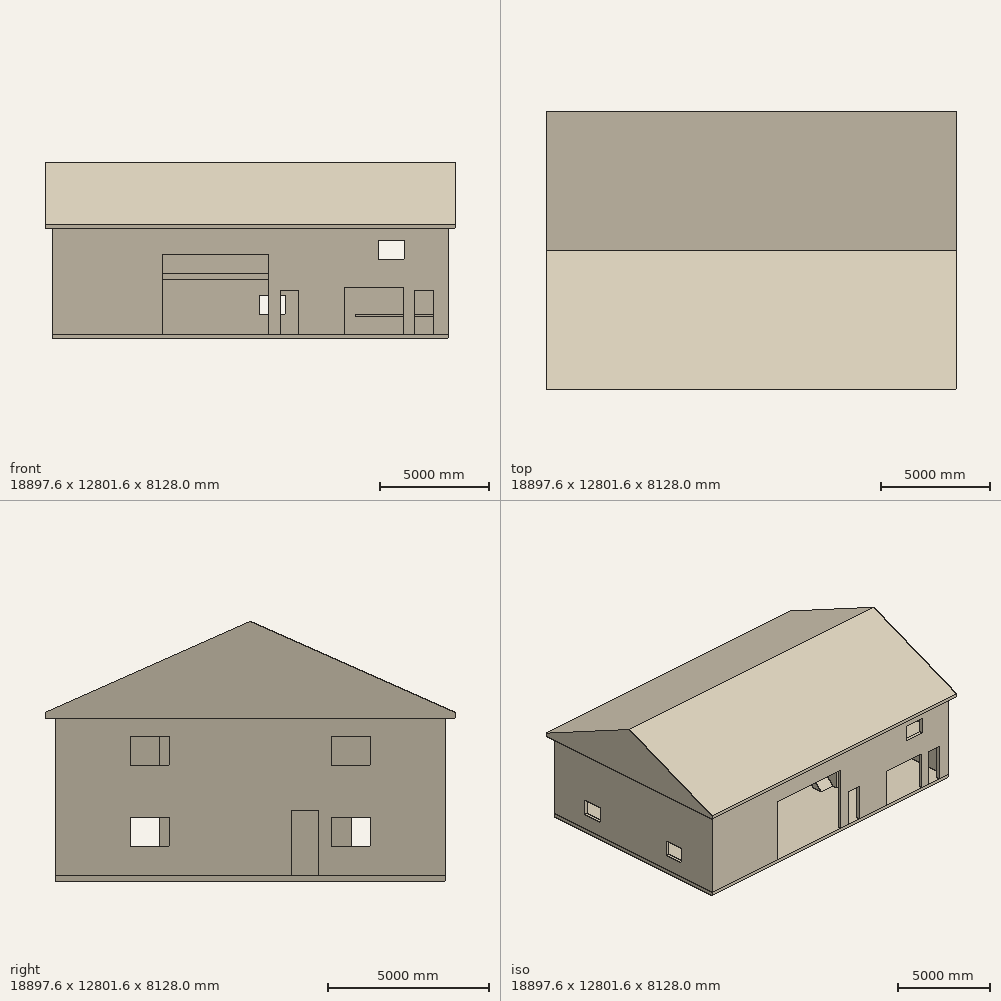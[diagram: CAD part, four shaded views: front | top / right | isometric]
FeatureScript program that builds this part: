
annotation { "Feature Type Name" : "Feature", "Feature Type Description" : "" }
export const myFeature = defineFeature(function(context is Context, id is Id, definition is map)
    precondition{}
    {
        {
            var Q0;
            Q0=qCreatedBy(makeId("Top.planeOp"),FACE);
            var sketch = newSketch(context, id + "F0", { "sketchPlane" : qUnion([Q0])});
            skLineSegment(sketch, "E0.bottom", {"start": v(-9144, 6096) * mm, "end": v(9144, 6096) * mm});
            skLineSegment(sketch, "E0.top", {"start": v(-9144, -6096) * mm, "end": v(9144, -6096) * mm});
            skLineSegment(sketch, "E0.left", {"start": v(-9144, 6096) * mm, "end": v(-9144, -6096) * mm});
            skLineSegment(sketch, "E0.right", {"start": v(9144, 6096) * mm, "end": v(9144, -6096) * mm});
            skLineSegment(sketch, "E1", {"start": v(-9144, 6096) * mm, "end": v(9144, -6096) * mm, "construction": true});
            skSolve(sketch);
        }
        {
            var Q0;
            Q0=makeQuery(id+"F0.imprint","IMPRINT",FACE,{"disambiguationData":[TD([[makeQuery(id+"F0.imprint","IMPRINT",EDGE,{"derivedFrom":sQuery(id+"F0.wireOp",EDGE,"E0.bottom")}),-1.0]])]});
            extrude(context, id + "F1", {"entities" : qUnion([Q0]), "depth" : 203.2 * mm, "offsetDistance" : 25.4 * mm});
        }
        {
            var Q0;
            Q0=makeQuery(id+"F1.opExtrude","CAP_FACE",FACE,{"disambiguationData":[OSD([sQuery(id+"F0.wireOp",EDGE,"E0.bottom"),sQuery(id+"F0.wireOp",EDGE,"E0.top"),sQuery(id+"F0.wireOp",EDGE,"E0.left"),sQuery(id+"F0.wireOp",EDGE,"E0.right")])],"isStart":false});
            var sketch = newSketch(context, id + "F2", { "sketchPlane" : qUnion([Q0])});
            skLineSegment(sketch, "E2.0", {"start": v(-9144, 6096) * mm, "end": v(9144, 6096) * mm});
            skLineSegment(sketch, "E2.1", {"start": v(-9144, 6096) * mm, "end": v(-9144, -6096) * mm});
            skLineSegment(sketch, "E2.2", {"start": v(-9144, -6096) * mm, "end": v(9144, -6096) * mm});
            skLineSegment(sketch, "E2.3", {"start": v(9144, 6096) * mm, "end": v(9144, -6096) * mm});
            skLineSegment(sketch, "E3.0", {"start": v(-8940.8, 5892.8) * mm, "end": v(8940.8, 5892.8) * mm});
            skLineSegment(sketch, "E3.1", {"start": v(-8940.8, 5892.8) * mm, "end": v(-8940.8, -5892.8) * mm});
            skLineSegment(sketch, "E3.2", {"start": v(-8940.8, -5892.8) * mm, "end": v(8940.8, -5892.8) * mm});
            skLineSegment(sketch, "E3.3", {"start": v(8940.8, 5892.8) * mm, "end": v(8940.8, -5892.8) * mm});
            skSolve(sketch);
        }
        {
            var Q0;
            Q0=qSketchRegion(id+"F2",true);
            extrude(context, id + "F3", {"entities" : qUnion([Q0]), "depth" : 4876.8 * mm, "offsetDistance" : 25.4 * mm});
        }
        {
            var Q0;
            Q0=qCreatedBy(makeId("Right.planeOp"),FACE);
            var sketch = newSketch(context, id + "F4", { "sketchPlane" : qUnion([Q0])});
            skLineSegment(sketch, "E4.0", {"start": v(6400.8, 5080) * mm, "end": v(-6400.8, 5080) * mm});
            skLineSegment(sketch, "E5", {"start": v(-6400.8, 5080) * mm, "end": v(-6400.8, 5283.2) * mm});
            skLineSegment(sketch, "E6", {"start": v(-6400.8, 5283.2) * mm, "end": v(0, 8128) * mm});
            skLineSegment(sketch, "E7", {"start": v(0, 8128) * mm, "end": v(6400.8, 5283.2) * mm});
            skLineSegment(sketch, "E8", {"start": v(6400.8, 5283.2) * mm, "end": v(6400.8, 5080) * mm});
            skSolve(sketch);
        }
        {
            var Q0;
            Q0=qSketchRegion(id+"F4",true);
            var Q1;
            Q1=makeQuery(id+"F3.opExtrude","SWEPT_FACE",FACE,{"disambiguationData":[OSD([sQuery(id+"F2.wireOp",EDGE,"E2.3")])]});
            var Q2;
            Q2=makeQuery(id+"F3.opExtrude","SWEPT_FACE",FACE,{"disambiguationData":[OSD([sQuery(id+"F2.wireOp",EDGE,"E2.1")])]});
            extrude(context, id + "F5", {"entities" : qUnion([Q0]), "endBound" : BoundingType.UP_TO_SURFACE, "depth" : 25.4 * mm, "endBoundEntityFace" : qUnion([Q1]), "hasOffset" : true, "offsetDistance" : -304.8 * mm, "hasSecondDirection" : true, "secondDirectionBound" : SecondDirectionBoundingType.UP_TO_SURFACE, "secondDirectionOppositeDirection" : true, "secondDirectionDepth" : 25.4 * mm, "secondDirectionBoundEntityFace" : qUnion([Q2]), "hasSecondDirectionOffset" : true, "secondDirectionOffsetDistance" : -304.8 * mm});
        }
        {
            var Q0;
            Q0=makeQuery(id+"F1.opExtrude","CAP_FACE",FACE,{"disambiguationData":[OSD([sQuery(id+"F0.wireOp",EDGE,"E0.bottom"),sQuery(id+"F0.wireOp",EDGE,"E0.top"),sQuery(id+"F0.wireOp",EDGE,"E0.left"),sQuery(id+"F0.wireOp",EDGE,"E0.right")])],"isStart":false});
            var sketch = newSketch(context, id + "F6", { "sketchPlane" : qUnion([Q0])});
            skLineSegment(sketch, "E9", {"start": v(3759.2, -5892.8) * mm, "end": v(3759.2, 5892.8) * mm});
            skLineSegment(sketch, "E10.0", {"start": v(3911.6, -5892.8) * mm, "end": v(3911.6, 203.2) * mm});
            skLineSegment(sketch, "E11", {"start": v(3911.6, 355.6) * mm, "end": v(8940.8, 355.6) * mm});
            skLineSegment(sketch, "E12.0", {"start": v(3911.6, 203.2) * mm, "end": v(8940.8, 203.2) * mm});
            skLineSegment(sketch, "E13.trimOffspring", {"start": v(3911.6, 355.6) * mm, "end": v(3911.6, 5892.8) * mm});
            skLineSegment(sketch, "E14", {"start": v(3759.2, -5892.8) * mm, "end": v(3911.6, -5892.8) * mm});
            skLineSegment(sketch, "E15", {"start": v(3759.2, 5892.8) * mm, "end": v(3911.6, 5892.8) * mm});
            skLineSegment(sketch, "E16", {"start": v(8940.8, 355.6) * mm, "end": v(8940.8, 203.2) * mm});
            skSolve(sketch);
        }
        {
            var Q0;
            Q0=qSketchRegion(id+"F6",true);
            extrude(context, id + "F7", {"entities" : qUnion([Q0]), "depth" : 2336.8 * mm, "offsetDistance" : 25.4 * mm});
        }
        {
            var Q0;
            Q0=makeQuery(id+"F7.opExtrude","CAP_FACE",FACE,{"disambiguationData":[OSD([sQuery(id+"F6.wireOp",EDGE,"E9"),sQuery(id+"F6.wireOp",EDGE,"E10.0"),sQuery(id+"F6.wireOp",EDGE,"E11"),sQuery(id+"F6.wireOp",EDGE,"E12.0"),sQuery(id+"F6.wireOp",EDGE,"E13.trimOffspring"),sQuery(id+"F6.wireOp",EDGE,"E14"),sQuery(id+"F6.wireOp",EDGE,"E15"),sQuery(id+"F6.wireOp",EDGE,"E16")])],"isStart":false});
            var sketch = newSketch(context, id + "F8", { "sketchPlane" : qUnion([Q0])});
            skLineSegment(sketch, "E17.0", {"start": v(3759.2, -5892.8) * mm, "end": v(3759.2, 5892.8) * mm});
            skLineSegment(sketch, "E18.0", {"start": v(8940.8, 5892.8) * mm, "end": v(8940.8, -5892.8) * mm});
            skLineSegment(sketch, "E19.0", {"start": v(3759.2, 5892.8) * mm, "end": v(8940.8, 5892.8) * mm});
            skLineSegment(sketch, "E20.0", {"start": v(3759.2, -5892.8) * mm, "end": v(8940.8, -5892.8) * mm});
            skPoint(sketch, "E21.orphan", {"position": v(-8940.8, -5892.8) * mm});
            skPoint(sketch, "E22.orphan", {"position": v(-8940.8, 5892.8) * mm});
            skSolve(sketch);
        }
        {
            var Q0;
            Q0=qSketchRegion(id+"F8",true);
            extrude(context, id + "F9", {"entities" : qUnion([Q0]), "depth" : 203.2 * mm, "offsetDistance" : 25.4 * mm});
        }
        {
            var Q0;
            Q0=makeQuery(id+"F3.opExtrude","SWEPT_FACE",FACE,{"disambiguationData":[OSD([sQuery(id+"F2.wireOp",EDGE,"E2.2")])]});
            var sketch = newSketch(context, id + "F10", { "sketchPlane" : qUnion([Q0])});
            skLineSegment(sketch, "E23.bottom", {"start": v(-4064, 203.2) * mm, "end": v(812.8, 203.2) * mm});
            skLineSegment(sketch, "E23.top", {"start": v(-4064, 3860.8) * mm, "end": v(812.8, 3860.8) * mm});
            skLineSegment(sketch, "E23.left", {"start": v(-4064, 203.2) * mm, "end": v(-4064, 3860.8) * mm});
            skLineSegment(sketch, "E23.right", {"start": v(812.8, 203.2) * mm, "end": v(812.8, 3860.8) * mm});
            skLineSegment(sketch, "E24.bottom", {"start": v(1371.6, 203.2) * mm, "end": v(2235.2, 203.2) * mm});
            skLineSegment(sketch, "E24.top", {"start": v(1371.6, 2235.2) * mm, "end": v(2235.2, 2235.2) * mm});
            skLineSegment(sketch, "E24.left", {"start": v(1371.6, 203.2) * mm, "end": v(1371.6, 2235.2) * mm});
            skLineSegment(sketch, "E24.right", {"start": v(2235.2, 203.2) * mm, "end": v(2235.2, 2235.2) * mm});
            skLineSegment(sketch, "E25.bottom", {"start": v(4318, 203.2) * mm, "end": v(7061.2, 203.2) * mm});
            skLineSegment(sketch, "E25.top", {"start": v(4318, 2336.8) * mm, "end": v(7061.2, 2336.8) * mm});
            skLineSegment(sketch, "E25.left", {"start": v(4318, 203.2) * mm, "end": v(4318, 2336.8) * mm});
            skLineSegment(sketch, "E25.right", {"start": v(7061.2, 203.2) * mm, "end": v(7061.2, 2336.8) * mm});
            skLineSegment(sketch, "E26.bottom", {"start": v(7569.2, 203.2) * mm, "end": v(8432.8, 203.2) * mm});
            skLineSegment(sketch, "E26.top", {"start": v(7569.2, 2235.2) * mm, "end": v(8432.8, 2235.2) * mm});
            skLineSegment(sketch, "E26.left", {"start": v(7569.2, 203.2) * mm, "end": v(7569.2, 2235.2) * mm});
            skLineSegment(sketch, "E26.right", {"start": v(8432.8, 203.2) * mm, "end": v(8432.8, 2235.2) * mm});
            skLineSegment(sketch, "E27.bottom", {"start": v(5892.8, 4546.6) * mm, "end": v(7112, 4546.6) * mm});
            skLineSegment(sketch, "E27.top", {"start": v(5892.8, 3632.2) * mm, "end": v(7112, 3632.2) * mm});
            skLineSegment(sketch, "E27.left", {"start": v(5892.8, 4546.6) * mm, "end": v(5892.8, 3632.2) * mm});
            skLineSegment(sketch, "E27.right", {"start": v(7112, 4546.6) * mm, "end": v(7112, 3632.2) * mm});
            skSolve(sketch);
        }
        {
            var Q0;
            Q0=qSketchRegion(id+"F10",true);
            extrude(context, id + "F11", {"entities" : qUnion([Q0]), "operationType" : NewBodyOperationType.REMOVE, "endBound" : BoundingType.UP_TO_NEXT, "oppositeDirection" : true, "depth" : 25.4 * mm, "offsetDistance" : 25.4 * mm});
        }
        {
            var Q0;
            Q0=makeQuery(id+"F3.opExtrude","SWEPT_FACE",FACE,{"disambiguationData":[OSD([sQuery(id+"F2.wireOp",EDGE,"E2.3")])]});
            var sketch = newSketch(context, id + "F12", { "sketchPlane" : qUnion([Q0])});
            skLineSegment(sketch, "E28.bottom", {"start": v(-5588, 203.2) * mm, "end": v(-4724.4, 203.2) * mm, "construction": true});
            skLineSegment(sketch, "E28.top", {"start": v(-5588, 2235.2) * mm, "end": v(-4724.4, 2235.2) * mm, "construction": true});
            skLineSegment(sketch, "E28.left", {"start": v(-5588, 203.2) * mm, "end": v(-5588, 2235.2) * mm, "construction": true});
            skLineSegment(sketch, "E28.right", {"start": v(-4724.4, 203.2) * mm, "end": v(-4724.4, 2235.2) * mm, "construction": true});
            skLineSegment(sketch, "E29.bottom", {"start": v(1270, 203.2) * mm, "end": v(2133.6, 203.2) * mm});
            skLineSegment(sketch, "E29.top", {"start": v(1270, 2235.2) * mm, "end": v(2133.6, 2235.2) * mm});
            skLineSegment(sketch, "E29.left", {"start": v(1270, 203.2) * mm, "end": v(1270, 2235.2) * mm});
            skLineSegment(sketch, "E29.right", {"start": v(2133.6, 203.2) * mm, "end": v(2133.6, 2235.2) * mm});
            skSolve(sketch);
        }
        {
            var Q0;
            Q0=qSketchRegion(id+"F12",true);
            extrude(context, id + "F13", {"entities" : qUnion([Q0]), "operationType" : NewBodyOperationType.REMOVE, "endBound" : BoundingType.UP_TO_NEXT, "oppositeDirection" : true, "depth" : 25.4 * mm, "offsetDistance" : 25.4 * mm});
        }
        {
            var Q0;
            Q0=makeQuery(id+"F7.opExtrude","SWEPT_FACE",FACE,{"disambiguationData":[OSD([sQuery(id+"F6.wireOp",EDGE,"E9")])]});
            var sketch = newSketch(context, id + "F14", { "sketchPlane" : qUnion([Q0])});
            skLineSegment(sketch, "E30", {"start": v(1965.26, 203.2) * mm, "end": v(-371.54, 2540) * mm});
            skLineSegment(sketch, "E31", {"start": v(0, 2743.2) * mm, "end": v(2540, 203.2) * mm});
            skLineSegment(sketch, "E32", {"start": v(-574.74, 2743.2) * mm, "end": v(0, 2743.2) * mm});
            skLineSegment(sketch, "E33", {"start": v(2540, 203.2) * mm, "end": v(1965.26, 203.2) * mm});
            skLineSegment(sketch, "E34.bottom", {"start": v(2955.8, 203.2) * mm, "end": v(5394.2, 203.2) * mm, "construction": true});
            skLineSegment(sketch, "E34.top", {"start": v(2955.8, 2336.8) * mm, "end": v(5394.2, 2336.8) * mm, "construction": true});
            skLineSegment(sketch, "E34.left", {"start": v(2955.8, 203.2) * mm, "end": v(2955.8, 2336.8) * mm, "construction": true});
            skLineSegment(sketch, "E34.right", {"start": v(5394.2, 203.2) * mm, "end": v(5394.2, 2336.8) * mm, "construction": true});
            skLineSegment(sketch, "E35.bottom", {"start": v(-4403.76, 203.2) * mm, "end": v(-1965.36, 203.2) * mm, "construction": true});
            skLineSegment(sketch, "E35.top", {"start": v(-4403.76, 2336.8) * mm, "end": v(-1965.36, 2336.8) * mm, "construction": true});
            skLineSegment(sketch, "E35.left", {"start": v(-4403.76, 203.2) * mm, "end": v(-4403.76, 2336.8) * mm, "construction": true});
            skLineSegment(sketch, "E35.right", {"start": v(-1965.36, 203.2) * mm, "end": v(-1965.36, 2336.8) * mm, "construction": true});
            skLineSegment(sketch, "E36", {"start": v(-1219.2, 2540) * mm, "end": v(-1219.2, 2743.2) * mm});
            skLineSegment(sketch, "E37", {"start": v(-1219.2, 2743.2) * mm, "end": v(-574.74, 2743.2) * mm});
            skLineSegment(sketch, "E38", {"start": v(-1219.2, 2540) * mm, "end": v(-371.54, 2540) * mm});
            skSolve(sketch);
        }
        {
            var Q0;
            Q0=qSketchRegion(id+"F14",true);
            extrude(context, id + "F15", {"entities" : qUnion([Q0]), "depth" : 914.4 * mm, "offsetDistance" : 25.4 * mm});
        }
        {
            var Q0;
            Q0=makeQuery(id+"F7.opExtrude","SWEPT_FACE",FACE,{"disambiguationData":[OSD([sQuery(id+"F6.wireOp",EDGE,"E9")])]});
            var sketch = newSketch(context, id + "F16", { "sketchPlane" : qUnion([Q0])});
            skLineSegment(sketch, "E39.bottom", {"start": v(-5588, 203.2) * mm, "end": v(-3149.6, 203.2) * mm});
            skLineSegment(sketch, "E39.top", {"start": v(-5588, 2336.8) * mm, "end": v(-3149.6, 2336.8) * mm});
            skLineSegment(sketch, "E39.left", {"start": v(-5588, 203.2) * mm, "end": v(-5588, 2336.8) * mm});
            skLineSegment(sketch, "E39.right", {"start": v(-3149.6, 203.2) * mm, "end": v(-3149.6, 2336.8) * mm});
            skLineSegment(sketch, "E40.bottom", {"start": v(2844.8, 203.2) * mm, "end": v(5283.2, 203.2) * mm});
            skLineSegment(sketch, "E40.top", {"start": v(2844.8, 2336.8) * mm, "end": v(5283.2, 2336.8) * mm});
            skLineSegment(sketch, "E40.left", {"start": v(2844.8, 203.2) * mm, "end": v(2844.8, 2336.8) * mm});
            skLineSegment(sketch, "E40.right", {"start": v(5283.2, 203.2) * mm, "end": v(5283.2, 2336.8) * mm});
            skSolve(sketch);
        }
        {
            var Q0;
            Q0=qSketchRegion(id+"F16",true);
            extrude(context, id + "F17", {"entities" : qUnion([Q0]), "operationType" : NewBodyOperationType.REMOVE, "endBound" : BoundingType.UP_TO_NEXT, "oppositeDirection" : true, "depth" : 25.4 * mm, "offsetDistance" : 25.4 * mm});
        }
        {
            var Q0;
            Q0=makeQuery(id+"F9.opExtrude","CAP_FACE",FACE,{"disambiguationData":[OSD([sQuery(id+"F8.wireOp",EDGE,"E17.0"),sQuery(id+"F8.wireOp",EDGE,"E18.0"),sQuery(id+"F8.wireOp",EDGE,"E19.0"),sQuery(id+"F8.wireOp",EDGE,"E20.0")])],"isStart":false});
            var sketch = newSketch(context, id + "F18", { "sketchPlane" : qUnion([Q0])});
            skLineSegment(sketch, "E41.0", {"start": v(3759.2, -5892.8) * mm, "end": v(3759.2, 5892.8) * mm});
            skLineSegment(sketch, "E42.0", {"start": v(3911.6, -5892.8) * mm, "end": v(3911.6, 5892.8) * mm});
            skLineSegment(sketch, "E43", {"start": v(3759.2, 5892.8) * mm, "end": v(3911.6, 5892.8) * mm});
            skLineSegment(sketch, "E44", {"start": v(3759.2, -5892.8) * mm, "end": v(3911.6, -5892.8) * mm});
            skSolve(sketch);
        }
        {
            var Q0;
            Q0=qSketchRegion(id+"F18",true);
            var Q1;
            Q1=makeQuery(id+"F3.opExtrude","CAP_FACE",FACE,{"disambiguationData":[OSD([sQuery(id+"F2.wireOp",EDGE,"E2.0"),sQuery(id+"F2.wireOp",EDGE,"E2.1"),sQuery(id+"F2.wireOp",EDGE,"E2.2"),sQuery(id+"F2.wireOp",EDGE,"E2.3"),sQuery(id+"F2.wireOp",EDGE,"E3.0"),sQuery(id+"F2.wireOp",EDGE,"E3.1"),sQuery(id+"F2.wireOp",EDGE,"E3.2"),sQuery(id+"F2.wireOp",EDGE,"E3.3")])],"isStart":false});
            extrude(context, id + "F19", {"entities" : qUnion([Q0]), "endBound" : BoundingType.UP_TO_SURFACE, "depth" : 25.4 * mm, "endBoundEntityFace" : qUnion([Q1]), "offsetDistance" : 25.4 * mm});
        }
        {
            var Q0;
            Q0=makeQuery(id+"F19.opExtrude","SWEPT_FACE",FACE,{"disambiguationData":[OSD([sQuery(id+"F18.wireOp",EDGE,"E41.0")])]});
            var sketch = newSketch(context, id + "F20", { "sketchPlane" : qUnion([Q0])});
            skLineSegment(sketch, "E45.bottom", {"start": v(-1219.2, 2743.2) * mm, "end": v(-355.6, 2743.2) * mm});
            skLineSegment(sketch, "E45.top", {"start": v(-1219.2, 4724.4) * mm, "end": v(-355.6, 4724.4) * mm});
            skLineSegment(sketch, "E45.left", {"start": v(-1219.2, 2743.2) * mm, "end": v(-1219.2, 4724.4) * mm});
            skLineSegment(sketch, "E45.right", {"start": v(-355.6, 2743.2) * mm, "end": v(-355.6, 4724.4) * mm});
            skLineSegment(sketch, "E46.bottom", {"start": v(2844.8, 2743.2) * mm, "end": v(5283.2, 2743.2) * mm});
            skLineSegment(sketch, "E46.top", {"start": v(2844.8, 4724.4) * mm, "end": v(5283.2, 4724.4) * mm});
            skLineSegment(sketch, "E46.left", {"start": v(2844.8, 2743.2) * mm, "end": v(2844.8, 4724.4) * mm});
            skLineSegment(sketch, "E46.right", {"start": v(5283.2, 2743.2) * mm, "end": v(5283.2, 4724.4) * mm});
            skSolve(sketch);
        }
        {
            var Q0;
            Q0=qSketchRegion(id+"F20",true);
            extrude(context, id + "F21", {"entities" : qUnion([Q0]), "operationType" : NewBodyOperationType.REMOVE, "endBound" : BoundingType.UP_TO_NEXT, "oppositeDirection" : true, "depth" : 25.4 * mm, "offsetDistance" : 25.4 * mm});
        }
        {
            var Q0;
            Q0=makeQuery(id+"F3.opExtrude","SWEPT_FACE",FACE,{"disambiguationData":[OSD([sQuery(id+"F2.wireOp",EDGE,"E3.0")])]});
            var sketch = newSketch(context, id + "F22", { "sketchPlane" : qUnion([Q0])});
            skLineSegment(sketch, "E47.bottom", {"start": v(-8940.8, 2997.2) * mm, "end": v(3759.2, 2997.2) * mm});
            skLineSegment(sketch, "E47.top", {"start": v(-8940.8, 2743.2) * mm, "end": v(3759.2, 2743.2) * mm});
            skLineSegment(sketch, "E47.left", {"start": v(-8940.8, 2997.2) * mm, "end": v(-8940.8, 2743.2) * mm});
            skLineSegment(sketch, "E47.right", {"start": v(3759.2, 2997.2) * mm, "end": v(3759.2, 2743.2) * mm});
            skSolve(sketch);
        }
        {
            var Q0;
            Q0=qSketchRegion(id+"F22",true);
            extrude(context, id + "F23", {"entities" : qUnion([Q0]), "depth" : 4572 * mm, "offsetDistance" : 25.4 * mm});
        }
        {
            var Q0;
            Q0=makeQuery(id+"F3.opExtrude","SWEPT_FACE",FACE,{"disambiguationData":[OSD([sQuery(id+"F2.wireOp",EDGE,"E3.1")])]});
            var sketch = newSketch(context, id + "F24", { "sketchPlane" : qUnion([Q0])});
            skLineSegment(sketch, "E48.bottom", {"start": v(5892.8, 3225.8) * mm, "end": v(-4064, 3225.8) * mm});
            skLineSegment(sketch, "E48.top", {"start": v(5892.8, 2971.8) * mm, "end": v(-4064, 2971.8) * mm});
            skLineSegment(sketch, "E48.left", {"start": v(5892.8, 3225.8) * mm, "end": v(5892.8, 2971.8) * mm});
            skLineSegment(sketch, "E48.right", {"start": v(-4064, 3225.8) * mm, "end": v(-4064, 2971.8) * mm});
            skSolve(sketch);
        }
        {
            var Q0;
            Q0=qSketchRegion(id+"F24",true);
            extrude(context, id + "F25", {"entities" : qUnion([Q0]), "depth" : 4876.8 * mm, "offsetDistance" : 25.4 * mm});
        }
        {
            var Q0;
            Q0=makeQuery(id+"F7.opExtrude","SWEPT_FACE",FACE,{"disambiguationData":[OSD([sQuery(id+"F6.wireOp",EDGE,"E11")])]});
            var sketch = newSketch(context, id + "F26", { "sketchPlane" : qUnion([Q0])});
            skLineSegment(sketch, "E49.bottom", {"start": v(-8940.8, 1879.6) * mm, "end": v(-3911.6, 1879.6) * mm});
            skLineSegment(sketch, "E49.top", {"start": v(-8940.8, 1828.8) * mm, "end": v(-3911.6, 1828.8) * mm});
            skLineSegment(sketch, "E49.left", {"start": v(-8940.8, 1879.6) * mm, "end": v(-8940.8, 1828.8) * mm});
            skLineSegment(sketch, "E49.right", {"start": v(-3911.6, 1879.6) * mm, "end": v(-3911.6, 1828.8) * mm});
            skLineSegment(sketch, "E50.bottom", {"start": v(-8940.8, 1320.8) * mm, "end": v(-3911.6, 1320.8) * mm});
            skLineSegment(sketch, "E50.top", {"start": v(-8940.8, 1270) * mm, "end": v(-3911.6, 1270) * mm});
            skLineSegment(sketch, "E50.left", {"start": v(-8940.8, 1320.8) * mm, "end": v(-8940.8, 1270) * mm});
            skLineSegment(sketch, "E50.right", {"start": v(-3911.6, 1320.8) * mm, "end": v(-3911.6, 1270) * mm});
            skLineSegment(sketch, "E51.bottom", {"start": v(-8940.8, 762) * mm, "end": v(-3911.6, 762) * mm});
            skLineSegment(sketch, "E51.top", {"start": v(-8940.8, 711.2) * mm, "end": v(-3911.6, 711.2) * mm});
            skLineSegment(sketch, "E51.left", {"start": v(-8940.8, 762) * mm, "end": v(-8940.8, 711.2) * mm});
            skLineSegment(sketch, "E51.right", {"start": v(-3911.6, 762) * mm, "end": v(-3911.6, 711.2) * mm});
            skSolve(sketch);
        }
        {
            var Q0;
            Q0=qSketchRegion(id+"F26",true);
            extrude(context, id + "F27", {"entities" : qUnion([Q0]), "operationType" : NewBodyOperationType.ADD, "depth" : 609.6 * mm, "offsetDistance" : 25.4 * mm});
        }
        {
            var Q0;
            Q0=makeQuery(id+"F7.opExtrude","SWEPT_FACE",FACE,{"disambiguationData":[OSD([sQuery(id+"F6.wireOp",EDGE,"E12.0")])]});
            var sketch = newSketch(context, id + "F28", { "sketchPlane" : qUnion([Q0])});
            skLineSegment(sketch, "E52.bottom", {"start": v(4826, 1117.6) * mm, "end": v(8940.8, 1117.6) * mm});
            skLineSegment(sketch, "E52.top", {"start": v(4826, 1041.4) * mm, "end": v(8940.8, 1041.4) * mm});
            skLineSegment(sketch, "E52.left", {"start": v(4826, 1117.6) * mm, "end": v(4826, 1041.4) * mm});
            skLineSegment(sketch, "E52.right", {"start": v(8940.8, 1117.6) * mm, "end": v(8940.8, 1041.4) * mm});
            skSolve(sketch);
        }
        {
            var Q0;
            Q0=qSketchRegion(id+"F28",true);
            extrude(context, id + "F29", {"entities" : qUnion([Q0]), "operationType" : NewBodyOperationType.ADD, "depth" : 914.4 * mm, "offsetDistance" : 25.4 * mm});
        }
        {
            var Q0;
            Q0=makeQuery(id+"F3.opExtrude","SWEPT_FACE",FACE,{"disambiguationData":[OSD([sQuery(id+"F2.wireOp",EDGE,"E2.0")])]});
            var sketch = newSketch(context, id + "F30", { "sketchPlane" : qUnion([Q0])});
            skLineSegment(sketch, "E53.0", {"start": v(-5892.8, 4546.6) * mm, "end": v(-5892.8, 3632.2) * mm});
            skLineSegment(sketch, "E53.1", {"start": v(-5892.8, 4546.6) * mm, "end": v(-7112, 4546.6) * mm});
            skLineSegment(sketch, "E53.2", {"start": v(-5892.8, 3632.2) * mm, "end": v(-7112, 3632.2) * mm});
            skLineSegment(sketch, "E53.3", {"start": v(-7112, 4546.6) * mm, "end": v(-7112, 3632.2) * mm});
            skLineSegment(sketch, "E54.bottom", {"start": v(-7112, 2006.6) * mm, "end": v(-5892.8, 2006.6) * mm});
            skLineSegment(sketch, "E54.top", {"start": v(-7112, 1092.2) * mm, "end": v(-5892.8, 1092.2) * mm});
            skLineSegment(sketch, "E54.left", {"start": v(-7112, 2006.6) * mm, "end": v(-7112, 1092.2) * mm});
            skLineSegment(sketch, "E54.right", {"start": v(-5892.8, 2006.6) * mm, "end": v(-5892.8, 1092.2) * mm});
            skLineSegment(sketch, "E55.bottom", {"start": v(-1625.6, 2006.6) * mm, "end": v(-406.4, 2006.6) * mm});
            skLineSegment(sketch, "E55.top", {"start": v(-1625.6, 1092.2) * mm, "end": v(-406.4, 1092.2) * mm});
            skLineSegment(sketch, "E55.left", {"start": v(-1625.6, 2006.6) * mm, "end": v(-1625.6, 1092.2) * mm});
            skLineSegment(sketch, "E55.right", {"start": v(-406.4, 2006.6) * mm, "end": v(-406.4, 1092.2) * mm});
            skLineSegment(sketch, "E56.bottom", {"start": v(5588, 2006.6) * mm, "end": v(6807.2, 2006.6) * mm});
            skLineSegment(sketch, "E56.top", {"start": v(5588, 1092.2) * mm, "end": v(6807.2, 1092.2) * mm});
            skLineSegment(sketch, "E56.left", {"start": v(5588, 2006.6) * mm, "end": v(5588, 1092.2) * mm});
            skLineSegment(sketch, "E56.right", {"start": v(6807.2, 2006.6) * mm, "end": v(6807.2, 1092.2) * mm});
            skSolve(sketch);
        }
        {
            var Q0;
            Q0=qSketchRegion(id+"F30",true);
            extrude(context, id + "F31", {"entities" : qUnion([Q0]), "operationType" : NewBodyOperationType.REMOVE, "endBound" : BoundingType.UP_TO_NEXT, "oppositeDirection" : true, "depth" : 25.4 * mm, "offsetDistance" : 25.4 * mm});
        }
        {
            var Q0;
            Q0=makeQuery(id+"F3.opExtrude","SWEPT_FACE",FACE,{"disambiguationData":[OSD([sQuery(id+"F2.wireOp",EDGE,"E2.1")])]});
            var sketch = newSketch(context, id + "F32", { "sketchPlane" : qUnion([Q0])});
            skLineSegment(sketch, "E57.bottom", {"start": v(-3759.2, 2006.6) * mm, "end": v(-2540, 2006.6) * mm});
            skLineSegment(sketch, "E57.top", {"start": v(-3759.2, 1092.2) * mm, "end": v(-2540, 1092.2) * mm});
            skLineSegment(sketch, "E57.left", {"start": v(-3759.2, 2006.6) * mm, "end": v(-3759.2, 1092.2) * mm});
            skLineSegment(sketch, "E57.right", {"start": v(-2540, 2006.6) * mm, "end": v(-2540, 1092.2) * mm});
            skLineSegment(sketch, "E58.bottom", {"start": v(2540, 2006.6) * mm, "end": v(3759.2, 2006.6) * mm});
            skLineSegment(sketch, "E58.top", {"start": v(2540, 1092.2) * mm, "end": v(3759.2, 1092.2) * mm});
            skLineSegment(sketch, "E58.left", {"start": v(2540, 2006.6) * mm, "end": v(2540, 1092.2) * mm});
            skLineSegment(sketch, "E58.right", {"start": v(3759.2, 2006.6) * mm, "end": v(3759.2, 1092.2) * mm});
            skSolve(sketch);
        }
        {
            var Q0;
            Q0=makeQuery(id+"F32.imprint","IMPRINT",FACE,{"disambiguationData":[TD([[makeQuery(id+"F32.imprint","IMPRINT",EDGE,{"derivedFrom":sQuery(id+"F32.wireOp",EDGE,"E57.bottom")}),-1.0]])]});
            var Q1;
            Q1=makeQuery(id+"F32.imprint","IMPRINT",FACE,{"disambiguationData":[TD([[makeQuery(id+"F32.imprint","IMPRINT",EDGE,{"derivedFrom":sQuery(id+"F32.wireOp",EDGE,"E58.bottom")}),-1.0]])]});
            extrude(context, id + "F33", {"entities" : qUnion([Q0, Q1]), "operationType" : NewBodyOperationType.REMOVE, "endBound" : BoundingType.UP_TO_NEXT, "oppositeDirection" : true, "depth" : 25.4 * mm, "offsetDistance" : 25.4 * mm});
        }
        {
            var Q0;
            Q0=makeQuery(id+"F3.opExtrude","SWEPT_FACE",FACE,{"disambiguationData":[OSD([sQuery(id+"F2.wireOp",EDGE,"E2.3")])]});
            var sketch = newSketch(context, id + "F34", { "sketchPlane" : qUnion([Q0])});
            skLineSegment(sketch, "E59.0", {"start": v(-2540, 2006.6) * mm, "end": v(-3759.2, 2006.6) * mm});
            skLineSegment(sketch, "E59.1", {"start": v(-2540, 2006.6) * mm, "end": v(-2540, 1092.2) * mm});
            skLineSegment(sketch, "E59.2", {"start": v(-2540, 1092.2) * mm, "end": v(-3759.2, 1092.2) * mm});
            skLineSegment(sketch, "E59.3", {"start": v(-3759.2, 2006.6) * mm, "end": v(-3759.2, 1092.2) * mm});
            skLineSegment(sketch, "E59.4", {"start": v(3759.2, 2006.6) * mm, "end": v(2540, 2006.6) * mm});
            skLineSegment(sketch, "E59.5", {"start": v(3759.2, 2006.6) * mm, "end": v(3759.2, 1092.2) * mm});
            skLineSegment(sketch, "E59.6", {"start": v(3759.2, 1092.2) * mm, "end": v(2540, 1092.2) * mm});
            skLineSegment(sketch, "E59.7", {"start": v(2540, 2006.6) * mm, "end": v(2540, 1092.2) * mm});
            skLineSegment(sketch, "E60.bottom", {"start": v(-3759.2, 4546.6) * mm, "end": v(-2540, 4546.6) * mm});
            skLineSegment(sketch, "E60.top", {"start": v(-3759.2, 3632.2) * mm, "end": v(-2540, 3632.2) * mm});
            skLineSegment(sketch, "E60.left", {"start": v(-3759.2, 4546.6) * mm, "end": v(-3759.2, 3632.2) * mm});
            skLineSegment(sketch, "E60.right", {"start": v(-2540, 4546.6) * mm, "end": v(-2540, 3632.2) * mm});
            skLineSegment(sketch, "E61.bottom", {"start": v(2540, 4546.6) * mm, "end": v(3759.2, 4546.6) * mm});
            skLineSegment(sketch, "E61.top", {"start": v(2540, 3632.2) * mm, "end": v(3759.2, 3632.2) * mm});
            skLineSegment(sketch, "E61.left", {"start": v(2540, 4546.6) * mm, "end": v(2540, 3632.2) * mm});
            skLineSegment(sketch, "E61.right", {"start": v(3759.2, 4546.6) * mm, "end": v(3759.2, 3632.2) * mm});
            skSolve(sketch);
        }
        {
            var Q0;
            Q0=qSketchRegion(id+"F34",true);
            extrude(context, id + "F35", {"entities" : qUnion([Q0]), "operationType" : NewBodyOperationType.REMOVE, "endBound" : BoundingType.UP_TO_NEXT, "oppositeDirection" : true, "depth" : 25.4 * mm, "offsetDistance" : 25.4 * mm});
        }
    });
